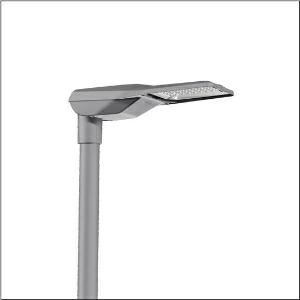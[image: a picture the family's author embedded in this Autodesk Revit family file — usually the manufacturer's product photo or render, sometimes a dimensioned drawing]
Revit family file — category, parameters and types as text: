
# Revit family: streetlight_sl_21_iq_mini___pl52_5xe2h31d08hb_f62b
name_source: partatom
category: Lighting Fixtures
units: mm (PartAtom-declared; Revit-internal decimal feet)

## family parameters
Cut with Voids When Loaded = No
Host = Face
Light Source = No
Part Type = Normal
Room Calculation Point = No
Round Connector Dimension = Use Diameter
Shared = No

## types (1)
- --- (1 x LED, 9290 lm, 70.9 W, 3000K)
    Apparent Load = 71 VA
    CIE Flux Codes = 27 59 98 100 100
    Color Rendering = 70
    Color Temperature = 3000K
    Default Elevation = 1800 mm
    Description = Streetlight SL 21 iQ mini, mast luminaire, primary light control with lens, of PMMA, primary optical cover: cover, of toughened safety glass, transparent, light distribution: PL52, light emission: direct distribution, primary light characteristic: asymmetric, installation type: post-top, side-entry, LED, High Power LED, rated luminous flux: 9.290lm, luminous efficacy: 131lm/W, light colour: 730, colour temperature: 3000K, control: Auto-Match, Temp-Guard, Lumen-Switch, Night-Set, Smart-Wire, Light-Fading, Desk-Remote (wireless, voltage-free reading and setting of iQ features in the workshop via application-optimized NFC function/RFID function), optimised constant luminous flux control (CLO 2.0), presetting dimming linear, mains connection: 220..240V, AC, 50/60Hz, start of lifetime: 71W, end of service life: 75W, reduction: 31W, luminaire housing, of diecast aluminium, powder-coated, Siteco® metallic grey (DB 702S), corrosivity category C5 mid according to DIN EN ISO 12944, please order mast flange separately, inclination adjustable: 0°, 5°, 10°, 15°, sealing non-destructively replaceable, multi-level sealing system, length: 628mm, width: 235mm, height: 110mm, mast flange for spigot size: 42mm (side-entry): 5XC10008XM4, 60/48mm (side-entry/post-top): 5XC10108XM2, 76/60mm (side-entry/post-top): 5XC10108XM1, protection rating (complete): IP66, insulation class (complete): insulation class II (safety insulation), certification: CE, ENEC, ENEC+, VDE, impact resistance: IK09, permissible operating ambient temperature for outdoor applications: -40..+50°C, standard-compliant lighting for roads and squares, packaging unit: 1 piece

Light Distribution: PL52
    Height = 110 mm
    Lamp = 1 x LED
    Lamp Light Flux = 9290 lm
    Lamp Power = 70.9 W
    Lamp count = 1
    Length = 625 mm
    Luminous efficacy = 131 lm/W
    Manufacturer = Siteco
    ModVariant = No
    Model = 5XE2H31D08HB
    Number of Poles = 1
    OnlyDefault = Yes
    Power Factor = 1
    Product Name = Streetlight SL 21 iQ mini | PL52
    Product group = mast luminaire | pylon top
    ProductGroupID = 6100
    Protection Class = Protection class II
    Protection Degree = IP 66
    RLX_Detail_Level = 1
    RLX_Emergency_Light_Flux = 0 lm
    RLX_Emergency_Type = 0
    RLX_Emergency_Type_DB = No
    RlxData = <blob elided: 101961 chars, md5=dbaaf88c>
    Socket = socket
    Standby Power = 0 W
    System Light Flux = 9290 lm
    System Power = 71 W
    Type Comments = factory setting: luminous flux: 100 % | dim-lin: 254 | 711 mA
    Type Image = l_1003519.jpg
    URL = http://relux.com
    VarID = @adj_108651
    Voltage = 0 V
    Weight = 0.00 kg
    Width = 234 mm

## geometry (parser evidence)
native form markers: Blend x4, Sweep x9
no freeform markers — native parametric forms only
